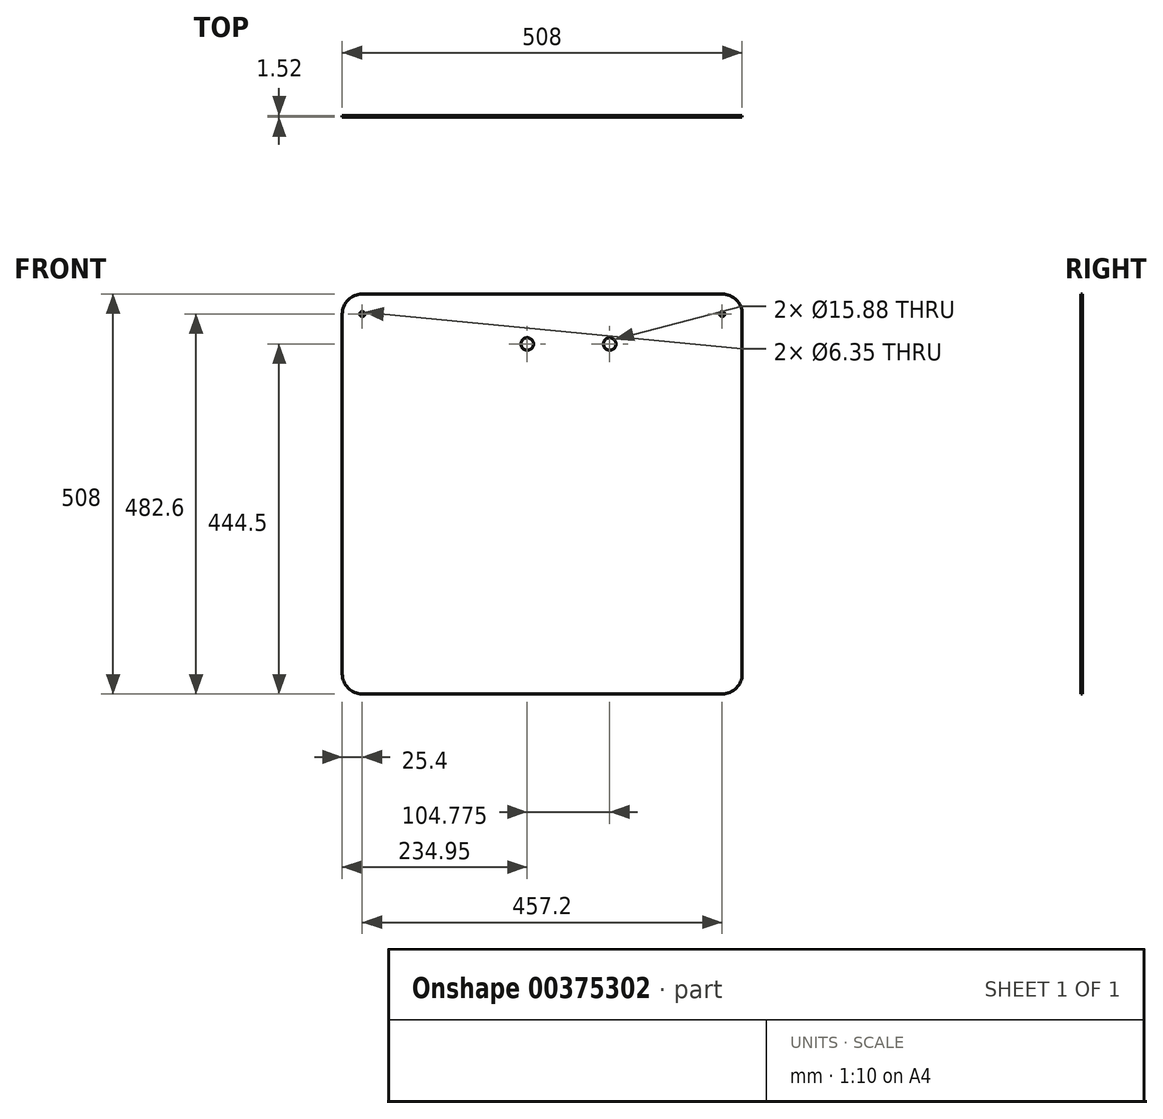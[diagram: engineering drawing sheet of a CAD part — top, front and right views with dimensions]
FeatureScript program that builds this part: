
annotation { "Feature Type Name" : "Feature", "Feature Type Description" : "" }
export const myFeature = defineFeature(function(context is Context, id is Id, definition is map)
    precondition{}
    {
        {
            var Q0;
            Q0=qCreatedBy(makeId("Front.planeOp"),FACE);
            var sketch = newSketch(context, id + "F0", { "sketchPlane" : qUnion([Q0])});
            skLineSegment(sketch, "E0.bottom", {"start": v(228.6, 254) * mm, "end": v(-228.6, 254) * mm});
            skLineSegment(sketch, "E0.top", {"start": v(228.6, -254) * mm, "end": v(-228.6, -254) * mm});
            skLineSegment(sketch, "E0.left", {"start": v(254, 228.6) * mm, "end": v(254, -228.6) * mm});
            skLineSegment(sketch, "E0.right", {"start": v(-254, 228.6) * mm, "end": v(-254, -228.6) * mm});
            skPoint(sketch, "E0.middle", {"position": v(0, 0) * mm});
            skPoint(sketch, "E1.visualSharp", {"position": v(-254, 254) * mm});
            skArc(sketch, "E1.filletArc", {"start": v(-228.6, 254) * mm, "mid": v(-246.56, 246.56) * mm, "end": v(-254, 228.6) * mm});
            skPoint(sketch, "E2.visualSharp", {"position": v(254, 254) * mm});
            skArc(sketch, "E2.filletArc", {"start": v(254, 228.6) * mm, "mid": v(246.56, 246.56) * mm, "end": v(228.6, 254) * mm});
            skPoint(sketch, "E3.visualSharp", {"position": v(254, -254) * mm});
            skArc(sketch, "E3.filletArc", {"start": v(228.6, -254) * mm, "mid": v(246.56, -246.56) * mm, "end": v(254, -228.6) * mm});
            skPoint(sketch, "E4.visualSharp", {"position": v(-254, -254) * mm});
            skArc(sketch, "E4.filletArc", {"start": v(-254, -228.6) * mm, "mid": v(-246.56, -246.56) * mm, "end": v(-228.6, -254) * mm});
            skLineSegment(sketch, "E5", {"start": v(-254, 190.5) * mm, "end": v(254, 190.5) * mm, "construction": true});
            skCircle(sketch, "E6", {"center": v(-19.05, 190.5) * mm, "radius": 7.94 * mm});
            skCircle(sketch, "E7", {"center": v(85.73, 190.5) * mm, "radius": 7.94 * mm});
            skCircle(sketch, "E8", {"center": v(-228.6, 228.6) * mm, "radius": 3.18 * mm});
            skCircle(sketch, "E9", {"center": v(228.6, 228.6) * mm, "radius": 3.18 * mm});
            skSolve(sketch);
        }
        {
            var Q0;
            Q0 = qSketchRegion(id + "F0", true);
            extrude(context, id + "F1", {"entities" : qUnion([Q0]), "depth" : 1.52 * mm, "offsetDistance" : 25.4 * mm});
        }
    });
